# Revit family: 09.Wichmann Akustikbox E_WAND
name_source: partatom
category: Mechanical Equipment
revit_build: Autodesk Revit 2018 (Build: 20170223_1515(x64)
units: mm (PartAtom-declared; Revit-internal decimal feet)

## family parameters
Always vertical = Yes
Classification = None
Cut with Voids When Loaded = No
Host = Wall
OmniClass Number = 23.30.20.00
OmniClass Title = Windows
Part Type = Normal
Room Calculation Point = No
Round Connector Dimension = Use Diameter
Shared = No

## types (6) — shared parameters
Bautiefe = 140 mm
H_i = 90 mm
H_rohbau = 160 mm
Height = 110 mm
Höhe = 110 mm
Werkstoff = Stahl

## per-type parameters (varying)
| type | B_i | B_rohbau | Breite | HAN | Width |
| Akustikbox E, 110x240x140 mm | 210 mm | 300 mm | 240 mm | ABE110240 | 240 mm |
| Akustikbox E, 110x280x140 mm | 250 mm | 340 mm | 280 mm | ABE110280 | 280 mm |
| Akustikbox E, 110x335x140 mm | 305 mm | 395 mm | 335 mm | ABE110335 | 335 mm |
| Akustikbox E, 110x435x140 mm | 405 mm | 495 mm | 435 mm | ABE110435 | 435 mm |
| Akustikbox E, 110x535x140 mm | 505 mm | 595 mm | 535 mm | ABE110535 | 535 mm |
| Akustikbox E, 110x640x140 mm | 610 mm | 700 mm | 640 mm | ABE110640 | 640 mm |

## geometry (parser evidence)
native form markers: Sweep x5
no freeform markers — native parametric forms only
